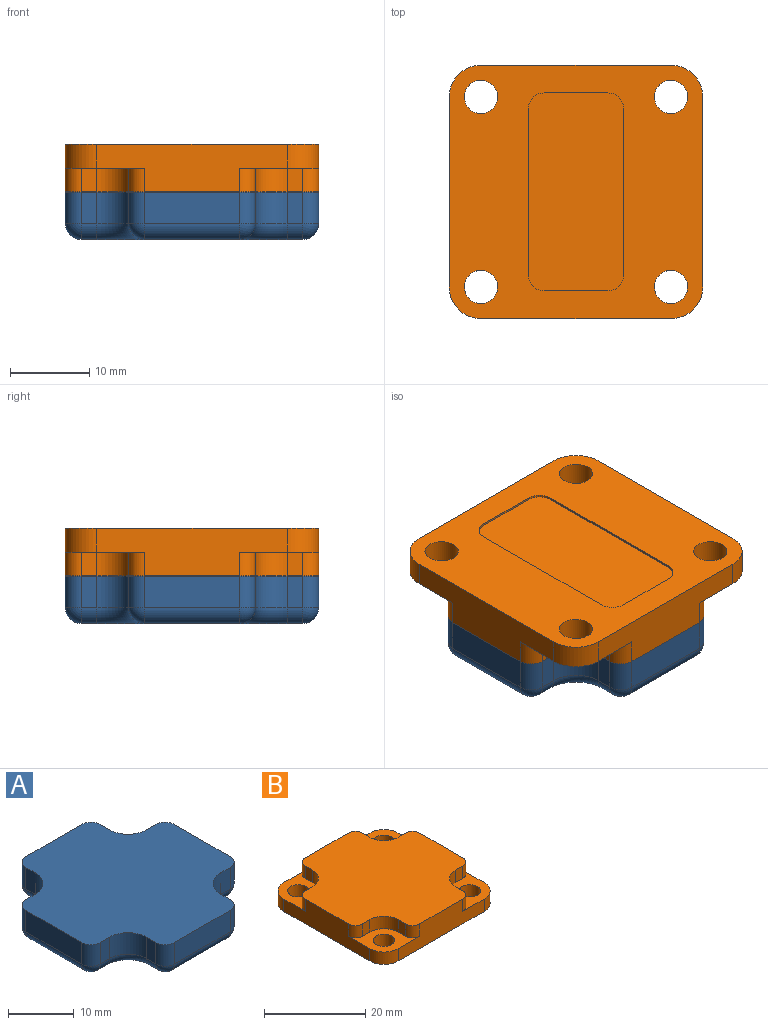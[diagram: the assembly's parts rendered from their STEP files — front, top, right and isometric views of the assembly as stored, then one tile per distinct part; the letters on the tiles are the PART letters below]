
ASSEMBLY  parts=2 mates=1
PART A: 50 faces, bbox 32x32x6 mm
  f0: cylinder r=2mm len=4mm, axis (0,0,-1), area 12.6mm2, adj f1,f5,f22,f47
  f1: plane 4x2mm, normal (1,0,0), area 8mm2, adj f0,f2,f5,f28
  f2: cylinder r=4mm len=4mm, axis (0,0,-1), area 25.1mm2, adj f1,f3,f5,f24
  f3: plane 4x2mm, normal (0,1,0), area 8mm2, adj f2,f4,f5,f23
  f4: cylinder r=2mm len=4mm, axis (0,0,-1), area 12.6mm2, adj f3,f5,f14,f44
  f5: plane 32x32mm, normal (0,0,1), area 774.9mm2, adj f0,f1,f2,f3,f4,f6,f7,f8
  f6: plane 4x2mm, normal (-1,0,0), area 8mm2, adj f5,f7,f30,f46
  f7: cylinder r=2mm len=4mm, axis (0,0,-1), area 12.6mm2, adj f5,f6,f8,f39
  f8: plane 12x4mm, normal (0,-1,0), area 48mm2, adj f5,f7,f9,f38
  f9: cylinder r=2mm len=4mm, axis (0,0,-1), area 12.6mm2, adj f5,f8,f10,f42
  f10: plane 4x2mm, normal (1,0,0), area 8mm2, adj f5,f9,f11,f40
  f11: cylinder r=4mm len=4mm, axis (0,0,-1), area 25.1mm2, adj f5,f10,f12,f33
  f12: plane 4x2mm, normal (0,-1,0), area 8mm2, adj f5,f11,f13,f41
  f13: cylinder r=2mm len=4mm, axis (0,0,-1), area 12.6mm2, adj f5,f12,f14,f31
  f14: plane 12x4mm, normal (1,0,0), area 48mm2, adj f4,f5,f13,f43
  f15: plane 28x28mm, normal (0,0,-1), area 558.9mm2, adj f23,f24,f25,f27,f28,f30,f32,f33
  f16: plane 12x4mm, normal (-1,0,0), area 48mm2, adj f5,f17,f35,f45
  f17: cylinder r=2mm len=4mm, axis (0,0,-1), area 12.6mm2, adj f5,f16,f18,f34
  f18: plane 4x2mm, normal (0,1,0), area 8mm2, adj f5,f17,f19,f49
  f19: cylinder r=4mm len=4mm, axis (0,0,-1), area 25.1mm2, adj f5,f18,f20,f48
  f20: plane 4x2mm, normal (-1,0,0), area 8mm2, adj f5,f19,f21,f27
  f21: cylinder r=2mm len=4mm, axis (0,0,-1), area 12.6mm2, adj f5,f20,f22,f29
  f22: plane 12x4mm, normal (0,1,0), area 48mm2, adj f0,f5,f21,f32
  f23: cylinder r=2mm len=2mm, axis (1,0,0), area 6.3mm2, adj f3,f15,f24,f44
  f24: torus R=6mm, axis (0,0,-1), area 23.3mm2, adj f2,f15,f23,f28
  f25: torus R=6mm, axis (0,0,-1), area 23.3mm2, adj f15,f30,f36,f46
  f26: plane 4x2mm, normal (0,-1,0), area 8mm2, adj f5,f36,f45,f46
  f27: cylinder r=2mm len=2mm, axis (0,1,0), area 6.3mm2, adj f15,f20,f29,f48
  f28: cylinder r=2mm len=2mm, axis (0,-1,0), area 6.3mm2, adj f1,f15,f24,f47
  f29: sphere r=2mm, area 6.3mm2, adj f21,f27,f32
  f30: cylinder r=2mm len=2mm, axis (0,1,0), area 6.3mm2, adj f6,f15,f25,f39
  f31: sphere r=2mm, area 6.3mm2, adj f13,f41,f43
  f32: cylinder r=2mm len=12mm, axis (1,0,0), area 37.7mm2, adj f15,f22,f29,f47
  f33: torus R=6mm, axis (0,0,-1), area 23.3mm2, adj f11,f15,f40,f41
  f34: sphere r=2mm, area 6.3mm2, adj f17,f35,f49
  f35: cylinder r=2mm len=12mm, axis (0,1,0), area 37.7mm2, adj f15,f16,f34,f37
  f36: cylinder r=2mm len=2mm, axis (-1,0,0), area 6.3mm2, adj f15,f25,f26,f37
  f37: sphere r=2mm, area 6.3mm2, adj f35,f36,f45
  f38: cylinder r=2mm len=12mm, axis (-1,0,0), area 37.7mm2, adj f8,f15,f39,f42
  f39: sphere r=2mm, area 6.3mm2, adj f7,f30,f38
  f40: cylinder r=2mm len=2mm, axis (0,-1,0), area 6.3mm2, adj f10,f15,f33,f42
  f41: cylinder r=2mm len=2mm, axis (-1,0,0), area 6.3mm2, adj f12,f15,f31,f33
  f42: sphere r=2mm, area 6.3mm2, adj f9,f38,f40
  f43: cylinder r=2mm len=12mm, axis (0,-1,0), area 37.7mm2, adj f14,f15,f31,f44
  f44: sphere r=2mm, area 6.3mm2, adj f4,f23,f43
  f45: cylinder r=2mm len=4mm, axis (0,0,-1), area 12.6mm2, adj f5,f16,f26,f37
  f46: cylinder r=4mm len=4mm, axis (0,0,-1), area 25.1mm2, adj f5,f6,f25,f26
  f47: sphere r=2mm, area 6.3mm2, adj f0,f28,f32
  f48: torus R=6mm, axis (0,0,-1), area 23.3mm2, adj f15,f19,f27,f49
  f49: cylinder r=2mm len=2mm, axis (1,0,0), area 6.3mm2, adj f15,f18,f34,f48
PART B: 47 faces, bbox 32x32x6 mm
  f0: cylinder r=2.1mm len=4.2mm, axis (0,0,-1), area 39.6mm2, adj f19,f44
  f1: cylinder r=4mm len=4mm, axis (0,0,-1), area 18.8mm2, adj f5,f19,f26,f45
  f2: cylinder r=2.1mm len=4.2mm, axis (0,0,-1), area 39.6mm2, adj f19,f43
  f3: cylinder r=2mm len=2mm, axis (0,0,-1), area 0.8mm2, adj f4,f19,f20,f24
  f4: plane 21x0.25mm, normal (-1,0,0), area 5.2mm2, adj f3,f19,f20,f36
  f5: plane 24x6mm, normal (0,-1,0), area 108mm2, adj f1,f9,f13,f19,f33,f35,f44,f45
  f6: plane 3x2mm, normal (0,1,0), area 6mm2, adj f9,f28,f39,f43
  f7: cylinder r=2.1mm len=4.2mm, axis (0,0,-1), area 39.6mm2, adj f18,f19
  f8: cylinder r=2.1mm len=4.2mm, axis (0,0,-1), area 39.6mm2, adj f19,f45
  f9: plane 32x32mm, normal (0,0,1), area 774.9mm2, adj f5,f6,f10,f11,f12,f16,f17,f21
  f10: plane 3x2mm, normal (0,-1,0), area 6mm2, adj f9,f31,f37,f45
  f11: cylinder r=2mm len=3mm, axis (0,0,-1), area 9.4mm2, adj f9,f29,f32,f43
  f12: plane 3x2mm, normal (-1,0,0), area 6mm2, adj f9,f17,f18,f30
  f13: cylinder r=4mm len=4mm, axis (0,0,-1), area 18.8mm2, adj f5,f19,f21,f44
  f14: cylinder r=2mm len=2mm, axis (0,0,-1), area 0.8mm2, adj f19,f20,f40,f42
  f15: cylinder r=2mm len=2mm, axis (0,0,-1), area 0.8mm2, adj f19,f20,f24,f42
  f16: plane 3x2mm, normal (0,1,0), area 6mm2, adj f9,f18,f22,f30
  f17: cylinder r=2mm len=3mm, axis (0,0,-1), area 9.4mm2, adj f9,f12,f18,f32
  f18: plane 10x10mm, normal (0,0,1), area 45mm2, adj f7,f12,f16,f17,f22,f25,f26,f30
  f19: plane 32x32mm, normal (0,0,-1), area 658.3mm2, adj f0,f1,f2,f3,f4,f5,f7,f8
  f20: plane 25x12mm, normal (0,0,-1), area 296.6mm2, adj f3,f4,f14,f15,f24,f36,f40,f42
  f21: plane 24x6mm, normal (1,0,0), area 108mm2, adj f9,f13,f19,f27,f39,f41,f43,f44
  f22: cylinder r=2mm len=3mm, axis (0,0,-1), area 9.4mm2, adj f9,f16,f18,f26
  f23: cylinder r=4mm len=4mm, axis (0,0,-1), area 18.8mm2, adj f9,f34,f44,f46
  f24: plane 8x0.25mm, normal (0,-1,0), area 2mm2, adj f3,f15,f19,f20
  f25: cylinder r=4mm len=4mm, axis (0,0,-1), area 18.8mm2, adj f18,f19,f26,f32
  f26: plane 24x6mm, normal (-1,0,0), area 108mm2, adj f1,f9,f18,f19,f22,f25,f37,f45
  f27: cylinder r=4mm len=4mm, axis (0,0,-1), area 18.8mm2, adj f19,f21,f32,f43
  f28: cylinder r=4mm len=4mm, axis (0,0,-1), area 18.8mm2, adj f6,f9,f29,f43
  f29: plane 3x2mm, normal (1,0,0), area 6mm2, adj f9,f11,f28,f43
  f30: cylinder r=4mm len=4mm, axis (0,0,-1), area 18.8mm2, adj f9,f12,f16,f18
  f31: cylinder r=4mm len=4mm, axis (0,0,-1), area 18.8mm2, adj f9,f10,f38,f45
  f32: plane 24x6mm, normal (0,1,0), area 108mm2, adj f9,f11,f17,f18,f19,f25,f27,f43
  f33: cylinder r=2mm len=3mm, axis (0,0,-1), area 9.4mm2, adj f5,f9,f38,f45
  f34: plane 3x2mm, normal (1,0,0), area 6mm2, adj f9,f23,f35,f44
  f35: cylinder r=2mm len=3mm, axis (0,0,-1), area 9.4mm2, adj f5,f9,f34,f44
  f36: cylinder r=2mm len=2mm, axis (0,0,-1), area 0.8mm2, adj f4,f19,f20,f40
  f37: cylinder r=2mm len=3mm, axis (0,0,-1), area 9.4mm2, adj f9,f10,f26,f45
  f38: plane 3x2mm, normal (-1,0,0), area 6mm2, adj f9,f31,f33,f45
  f39: cylinder r=2mm len=3mm, axis (0,0,-1), area 9.4mm2, adj f6,f9,f21,f43
  f40: plane 8x0.25mm, normal (0,1,0), area 2mm2, adj f14,f19,f20,f36
  f41: cylinder r=2mm len=3mm, axis (0,0,-1), area 9.4mm2, adj f9,f21,f44,f46
  f42: plane 21x0.25mm, normal (1,0,0), area 5.2mm2, adj f14,f15,f19,f20
  f43: plane 10x10mm, normal (0,0,1), area 45mm2, adj f2,f6,f11,f21,f27,f28,f29,f32
  f44: plane 10x10mm, normal (0,0,1), area 45mm2, adj f0,f5,f13,f21,f23,f34,f35,f41
  f45: plane 10x10mm, normal (0,0,1), area 45mm2, adj f1,f5,f8,f10,f26,f31,f33,f37
  f46: plane 3x2mm, normal (0,-1,0), area 6mm2, adj f9,f23,f41,f44
PLACE A t=(8.68,-0.8,-1.57)mm
PLACE B rot(axis=(0,1,0),180deg) t=(40.68,-0.8,10.43)mm
MATE fastened B.f35 <-> A.f7  axis (0,0,-1) through (18.68,1.2,4.43)mm
